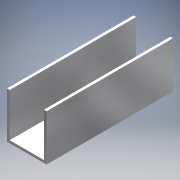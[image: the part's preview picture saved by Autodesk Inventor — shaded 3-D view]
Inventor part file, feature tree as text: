
AUTODESK INVENTOR PART (.ipt)
format: ipt  version: 2019 (Build 230136000, 136)  size: 101,376 bytes
history: native  units: in
note: dims shown in document units (in); Inventor stores cm internally (conversion verified against a paired STEP export)
features: extrude x1, sketch x1
ambient origin geometry x8: Origin, YZ Plane, XZ Plane, XY Plane, X Axis, Y Axis, Z Axis, Center Point
bodies: Solid1 (feature_tree)
feature tree (2):
  extrude  "Extrusion1"  Depth=12.0in TaperAngle=0.0deg
  sketch  "Sketch1"  dims[d2=0.25in d5=12.0in d6=0.0in d7=4.3755in d8=3.75in d9=0.25in d10=4.126in]
